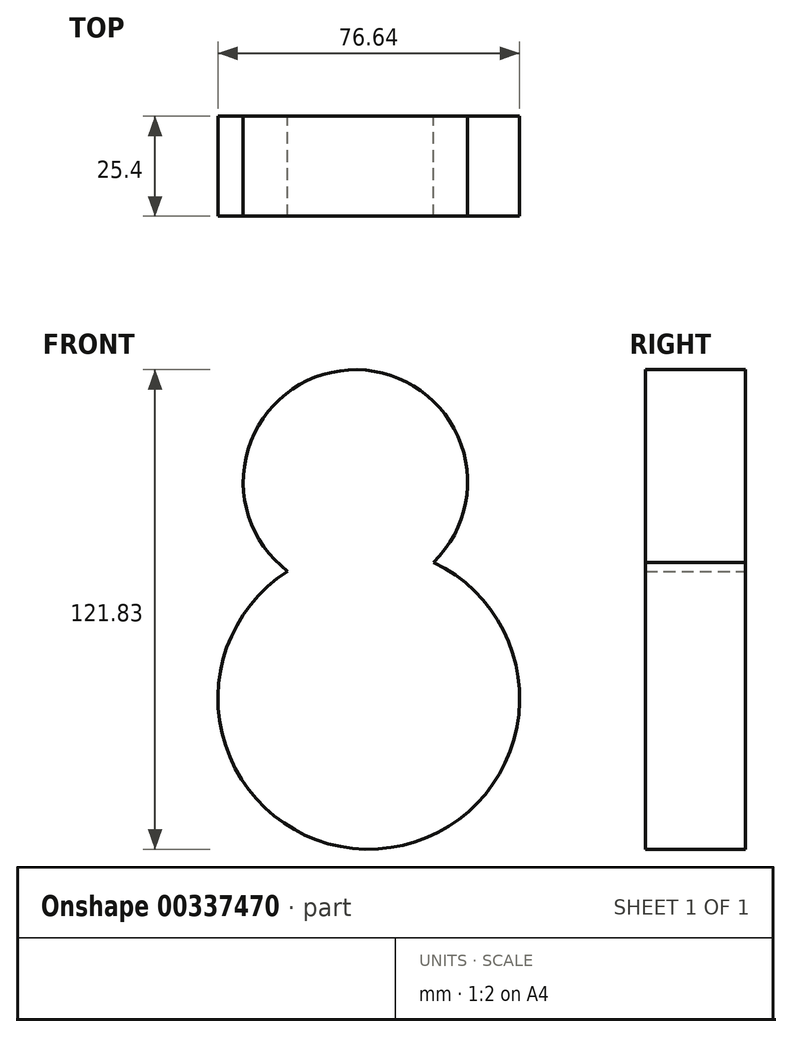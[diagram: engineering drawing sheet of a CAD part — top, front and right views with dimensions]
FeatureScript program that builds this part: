
annotation { "Feature Type Name" : "Feature", "Feature Type Description" : "" }
export const myFeature = defineFeature(function(context is Context, id is Id, definition is map)
    precondition{}
    {
        {
            var Q0;
            Q0=qCreatedBy(makeId("Front.planeOp"),FACE);
            var sketch = newSketch(context, id + "F0", { "sketchPlane" : qUnion([Q0])});
            skCircle(sketch, "E0", {"center": v(19.83, 55.02) * mm, "radius": 28.5 * mm});
            skCircle(sketch, "E1", {"center": v(23.22, 0) * mm, "radius": 38.32 * mm});
            skSolve(sketch);
        }
        {
            var Q0;
            Q0 = qSketchRegion(id + "F0", true);
            extrude(context, id + "F1", {"entities" : qUnion([Q0]), "depth" : 25.4 * mm});
        }
    });
